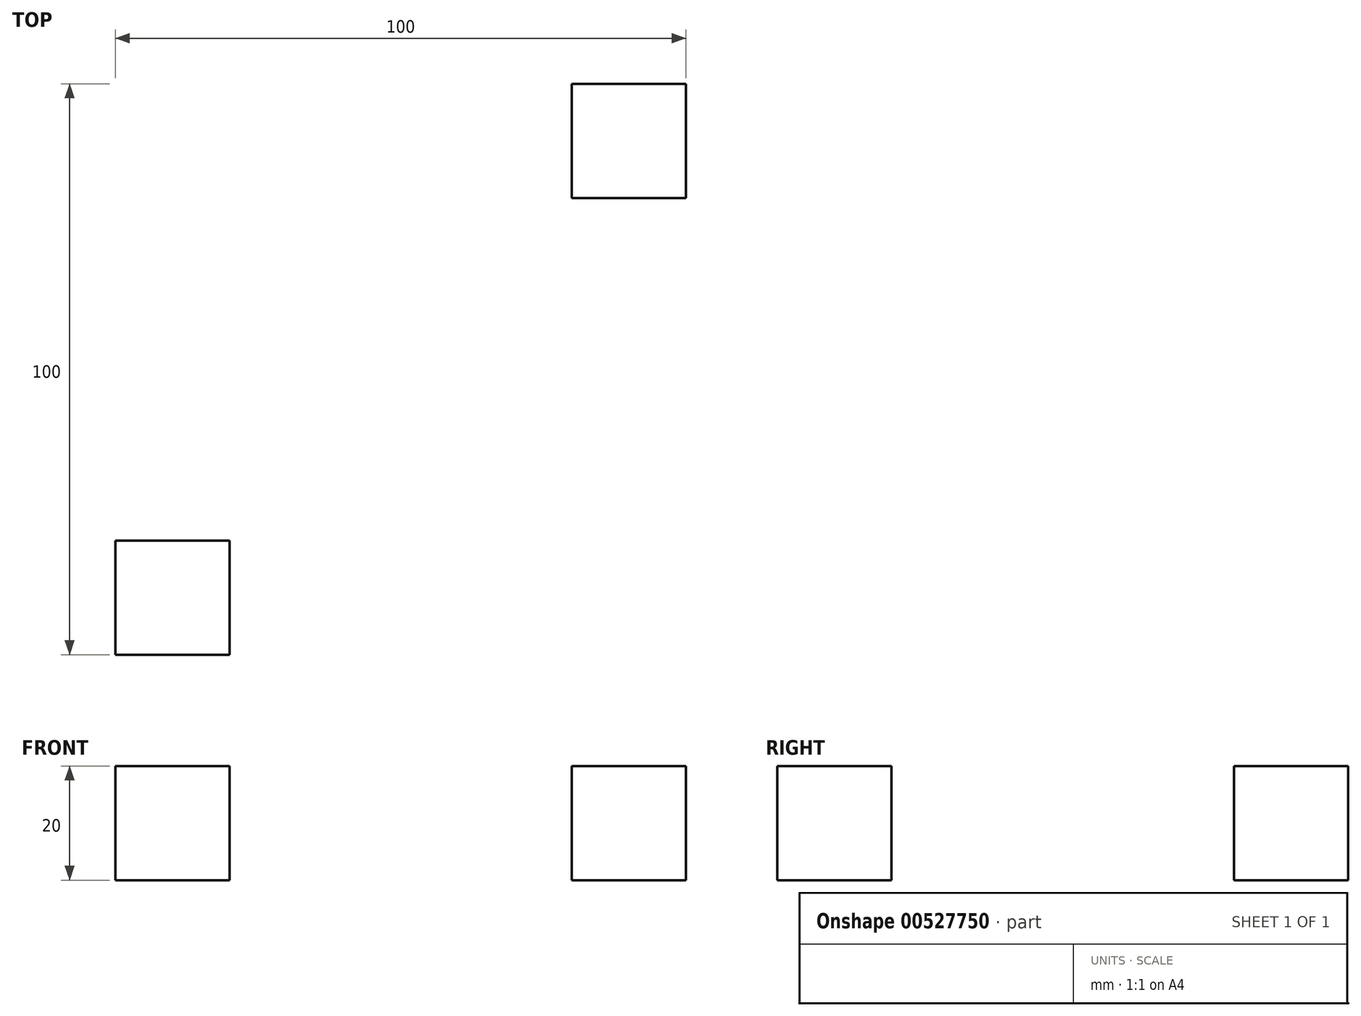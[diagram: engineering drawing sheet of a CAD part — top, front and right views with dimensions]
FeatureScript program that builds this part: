
annotation { "Feature Type Name" : "Feature", "Feature Type Description" : "" }
export const myFeature = defineFeature(function(context is Context, id is Id, definition is map)
    precondition{}
    {
        {
            var Q0;
            Q0=qCreatedBy(makeId("Top.planeOp"),FACE);
            var sketch = newSketch(context, id + "F0", { "sketchPlane" : qUnion([Q0])});
            skLineSegment(sketch, "E0.bottom", {"start": v(-50, -30) * mm, "end": v(-30, -30) * mm});
            skLineSegment(sketch, "E0.top", {"start": v(-50, -50) * mm, "end": v(-30, -50) * mm});
            skLineSegment(sketch, "E0.left", {"start": v(-50, -30) * mm, "end": v(-50, -50) * mm});
            skLineSegment(sketch, "E0.right", {"start": v(-30, -30) * mm, "end": v(-30, -50) * mm});
            skLineSegment(sketch, "E1", {"start": v(0, 0) * mm, "end": v(-30, 0) * mm, "construction": true});
            skLineSegment(sketch, "E2", {"start": v(0, 0) * mm, "end": v(0, -30) * mm, "construction": true});
            skLineSegment(sketch, "E3.MirrorCS", {"start": v(50, 30) * mm, "end": v(50, 50) * mm});
            skLineSegment(sketch, "E4.MirrorCS", {"start": v(30, 30) * mm, "end": v(30, 50) * mm});
            skLineSegment(sketch, "E5.MirrorCS", {"start": v(50, 30) * mm, "end": v(30, 30) * mm});
            skLineSegment(sketch, "E6.MirrorCS", {"start": v(50, 50) * mm, "end": v(30, 50) * mm});
            skSolve(sketch);
        }
        {
            var Q0;
            Q0=makeQuery(id+"F0.imprint","IMPRINT",FACE,{"disambiguationData":[TD([[makeQuery(id+"F0.imprint","IMPRINT",EDGE,{"derivedFrom":sQuery(id+"F0.wireOp",EDGE,"E0.bottom")}),-1.0]])]});
            var Q1;
            Q1=makeQuery(id+"F0.imprint","IMPRINT",FACE,{"disambiguationData":[TD([[makeQuery(id+"F0.imprint","IMPRINT",EDGE,{"derivedFrom":sQuery(id+"F0.wireOp",EDGE,"E3.MirrorCS")}),1.0]])]});
            extrude(context, id + "F1", {"entities" : qUnion([Q0, Q1]), "depth" : 20 * mm, "offsetDistance" : 25 * mm});
        }
    });
